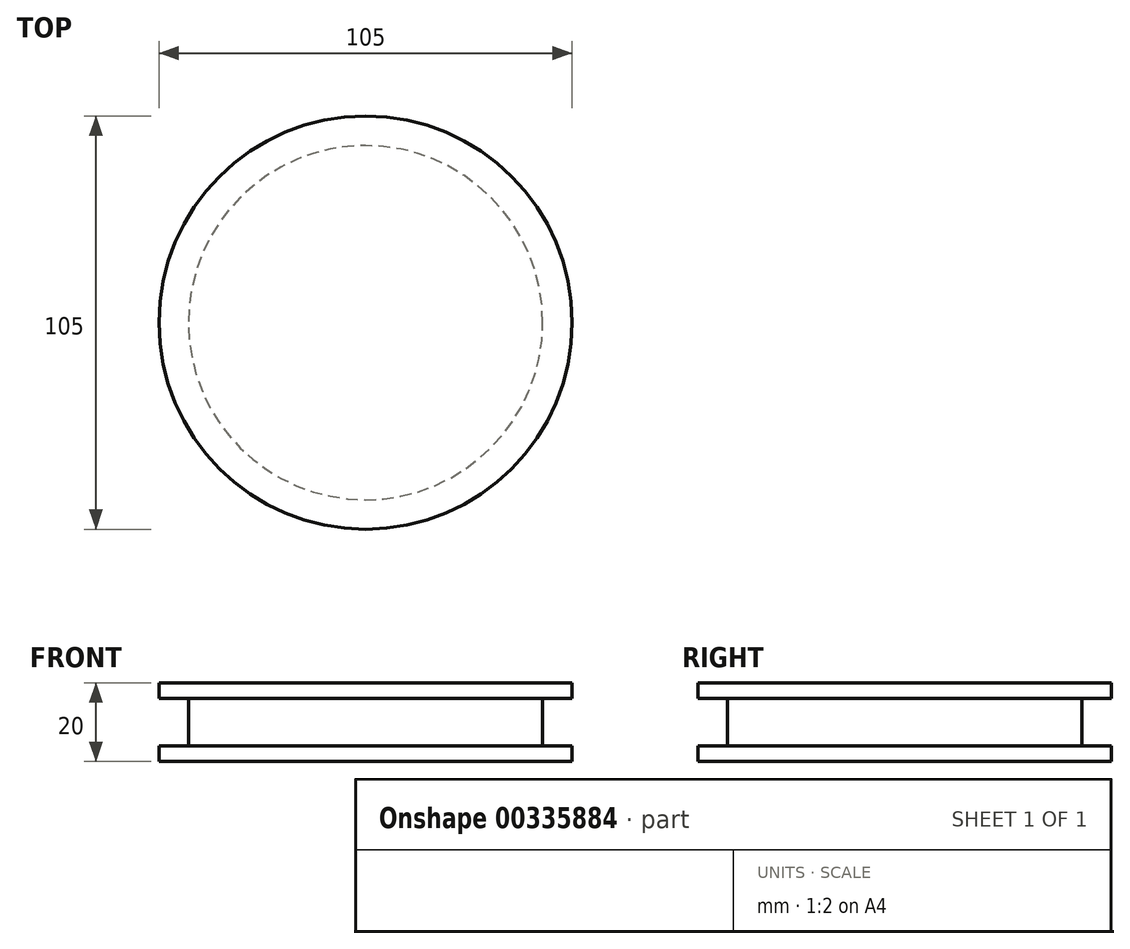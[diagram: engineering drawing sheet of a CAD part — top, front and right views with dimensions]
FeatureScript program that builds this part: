
annotation { "Feature Type Name" : "Feature", "Feature Type Description" : "" }
export const myFeature = defineFeature(function(context is Context, id is Id, definition is map)
    precondition{}
    {
        {
            assignVariable(context, id + "F0", {"name" : "alt_flange", "anyValue" : 4});
        }
        {
            assignVariable(context, id + "F1", {"name" : "alt_cinghia", "anyValue" : 12});
        }
        {
            var Q0;
            Q0=qCreatedBy(makeId("Top.planeOp"),FACE);
            var sketch = newSketch(context, id + "F2", { "sketchPlane" : qUnion([Q0])});
            skCircle(sketch, "E0", {"center": v(0, 0) * mm, "radius": 52.5 * mm});
            skSolve(sketch);
        }
        {
            var Q0;
            Q0=qSketchRegion(id+"F2",true);
            extrude(context, id + "F3", {"entities" : qUnion([Q0]), "depth" : (getVariable(context, 'alt_flange')) * mm});
        }
        {
            var Q0;
            Q0=qCreatedBy(makeId("Top.planeOp"),FACE);
            cPlane(context, id + "F4", {"entities" : qUnion([Q0]), "cplaneType" : CPlaneType.OFFSET, "offset" : (getVariable(context, 'alt_flange')) * mm, "width" : 150 * mm, "height" : 150 * mm});
        }
        {
            var Q0;
            Q0=qCreatedBy(id+"F4.planeOp",FACE);
            var sketch = newSketch(context, id + "F5", { "sketchPlane" : qUnion([Q0])});
            skCircle(sketch, "E1", {"center": v(0, 0) * mm, "radius": 45 * mm});
            skSolve(sketch);
        }
        {
            var Q0;
            Q0=qSketchRegion(id+"F5",true);
            extrude(context, id + "F6", {"entities" : qUnion([Q0]), "operationType" : NewBodyOperationType.ADD, "depth" : (getVariable(context, 'alt_cinghia')) * mm});
        }
        {
            var Q0;
            Q0=qCreatedBy(id+"F4.planeOp",FACE);
            cPlane(context, id + "F7", {"entities" : qUnion([Q0]), "cplaneType" : CPlaneType.OFFSET, "offset" : (getVariable(context, 'alt_cinghia')) * mm, "width" : 150 * mm, "height" : 150 * mm});
        }
        {
            var Q0;
            Q0=qCreatedBy(id+"F7.planeOp",FACE);
            var sketch = newSketch(context, id + "F8", { "sketchPlane" : qUnion([Q0])});
            skCircle(sketch, "E2", {"center": v(0, 0) * mm, "radius": 52.5 * mm});
            skSolve(sketch);
        }
        {
            var Q0;
            Q0=qSketchRegion(id+"F8",true);
            extrude(context, id + "F9", {"entities" : qUnion([Q0]), "operationType" : NewBodyOperationType.ADD, "depth" : (getVariable(context, 'alt_flange')) * mm});
        }
        {
            var Q0;
            Q0=makeQuery(id+"F3.opExtrude","SWEPT_BODY",BODY,{"disambiguationData":[OSD([sQuery(id+"F2.wireOp",EDGE,"E0")])]});
            transform(context, id + "F10", {"entities" : qUnion([Q0]), "transformType" : TransformType.TRANSLATION_3D, "dx" : 0 * mm, "dy" : 0 * mm, "dz" : (getVariable(context, 'alt_flange') * 2 + getVariable(context, 'alt_cinghia')) * mm, "makeCopy" : true});
        }
        {
            var Q0;
            Q0=makeQuery(id+"F10.opPattern","COPY",BODY,{"derivedFrom":makeQuery(id+"F3.opExtrude","SWEPT_BODY",BODY,{"disambiguationData":[OSD([sQuery(id+"F2.wireOp",EDGE,"E0")])]}),"instanceName":"1"});
            deleteBodies(context, id + "F11", {"entities" : qUnion([Q0])});
        }
        {
            var Q0;
            Q0=makeQuery(id+"F3.opExtrude","SWEPT_BODY",BODY,{"disambiguationData":[OSD([sQuery(id+"F2.wireOp",EDGE,"E0")])]});
            transform(context, id + "F12", {"entities" : qUnion([Q0]), "transformType" : TransformType.COPY});
        }
        {
            var Q0;
            Q0=makeQuery(id+"F12.opPattern","COPY",BODY,{"derivedFrom":makeQuery(id+"F3.opExtrude","SWEPT_BODY",BODY,{"disambiguationData":[OSD([sQuery(id+"F2.wireOp",EDGE,"E0")])]}),"instanceName":"1"});
            deleteBodies(context, id + "F13", {"entities" : qUnion([Q0])});
        }
        {
            var Q0;
            Q0=makeQuery(id+"F3.opExtrude","SWEPT_BODY",BODY,{"disambiguationData":[OSD([sQuery(id+"F2.wireOp",EDGE,"E0")])]});
            transform(context, id + "F14", {"entities" : qUnion([Q0]), "transformType" : TransformType.TRANSLATION_3D, "dx" : 0 * mm, "dy" : 0 * mm, "dz" : (getVariable(context, 'alt_flange') * 2 + getVariable(context, 'alt_cinghia')) * mm, "makeCopy" : false});
        }
    });
